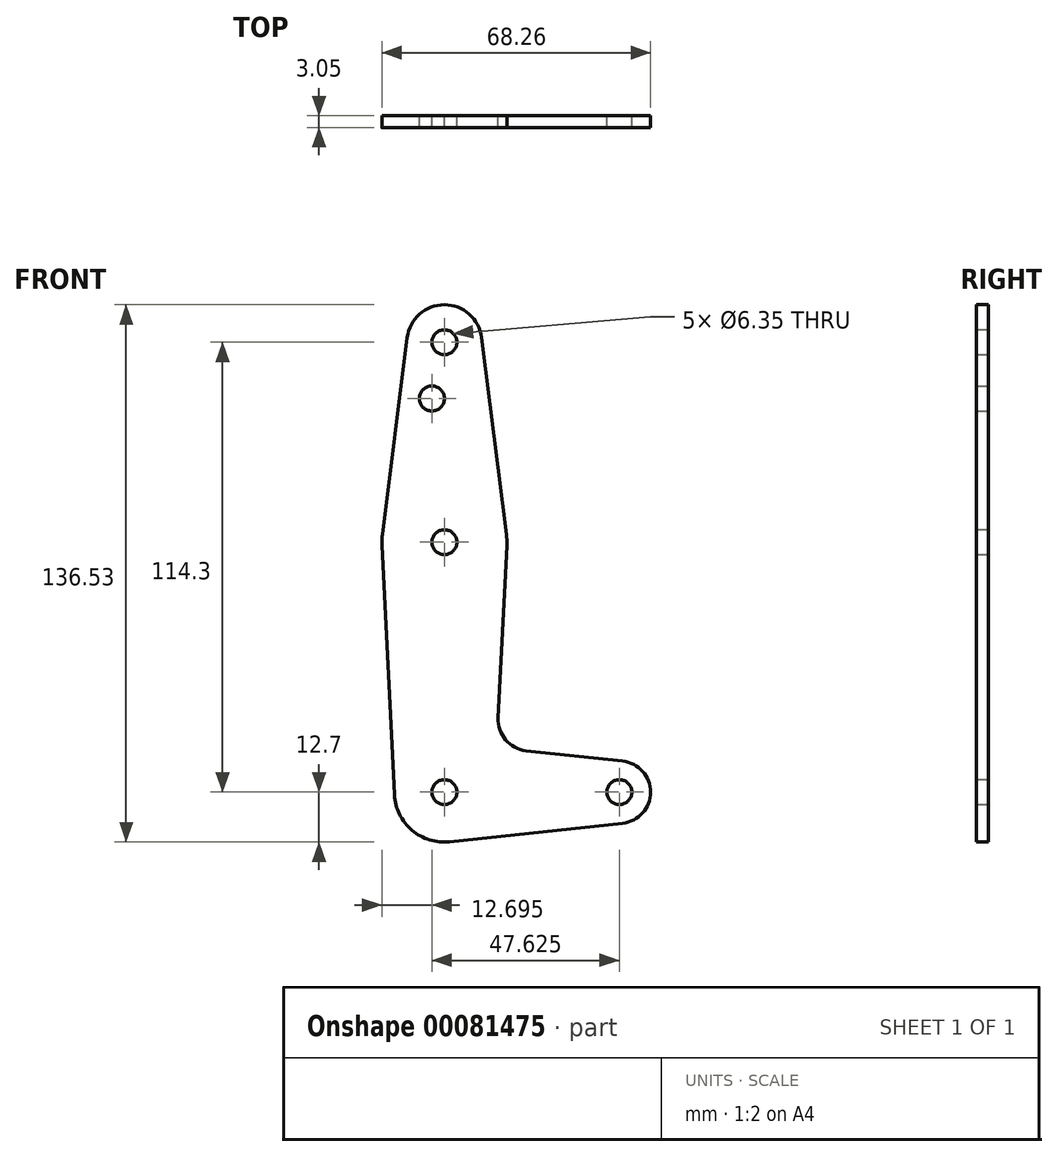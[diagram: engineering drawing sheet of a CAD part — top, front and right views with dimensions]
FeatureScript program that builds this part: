
annotation { "Feature Type Name" : "Feature", "Feature Type Description" : "" }
export const myFeature = defineFeature(function(context is Context, id is Id, definition is map)
    precondition{}
    {
        {
            var Q0;
            Q0=qCreatedBy(makeId("Front.planeOp"),FACE);
            var sketch = newSketch(context, id + "F0", { "sketchPlane" : qUnion([Q0])});
            skLineSegment(sketch, "E0", {"start": v(0, 0) * mm, "end": v(0, 114.3) * mm, "construction": true});
            skLineSegment(sketch, "E1", {"start": v(0, 0) * mm, "end": v(44.45, 0) * mm, "construction": true});
            skCircle(sketch, "E2", {"center": v(0, 114.3) * mm, "radius": 9.53 * mm});
            skCircle(sketch, "E3", {"center": v(0, 0) * mm, "radius": 12.7 * mm});
            skCircle(sketch, "E4", {"center": v(44.45, 0) * mm, "radius": 7.94 * mm});
            skCircle(sketch, "E5", {"center": v(0, 63.5) * mm, "radius": 15.88 * mm});
            skLineSegment(sketch, "E6", {"start": v(-15.86, 62.7) * mm, "end": v(-12.68, -0.64) * mm});
            skLineSegment(sketch, "E7", {"start": v(9.45, 115.5) * mm, "end": v(15.75, 65.48) * mm});
            skLineSegment(sketch, "E8", {"start": v(-9.45, 115.5) * mm, "end": v(-15.75, 65.48) * mm});
            skLineSegment(sketch, "E9", {"start": v(15.86, 62.7) * mm, "end": v(13.66, 18.84) * mm});
            skLineSegment(sketch, "E10", {"start": v(1.36, -12.63) * mm, "end": v(45.3, -7.9) * mm});
            skLineSegment(sketch, "E11", {"start": v(45.3, 7.9) * mm, "end": v(20.75, 10.54) * mm});
            skCircle(sketch, "E12", {"center": v(0, 114.3) * mm, "radius": 3.18 * mm});
            skCircle(sketch, "E13", {"center": v(-3.18, 100.03) * mm, "radius": 3.18 * mm});
            skCircle(sketch, "E14", {"center": v(0, 63.5) * mm, "radius": 3.18 * mm});
            skCircle(sketch, "E15", {"center": v(0, 0) * mm, "radius": 3.18 * mm});
            skCircle(sketch, "E16", {"center": v(44.45, 0) * mm, "radius": 3.18 * mm});
            skArc(sketch, "E17.filletArc", {"start": v(13.66, 18.84) * mm, "mid": v(15.55, 13.28) * mm, "end": v(20.75, 10.54) * mm});
            skSolve(sketch);
        }
        {
            var Q0;
            Q0 = qSketchRegion(id + "F0", true);
            extrude(context, id + "F1", {"entities" : qUnion([Q0]), "depth" : 3.05 * mm});
        }
    });
